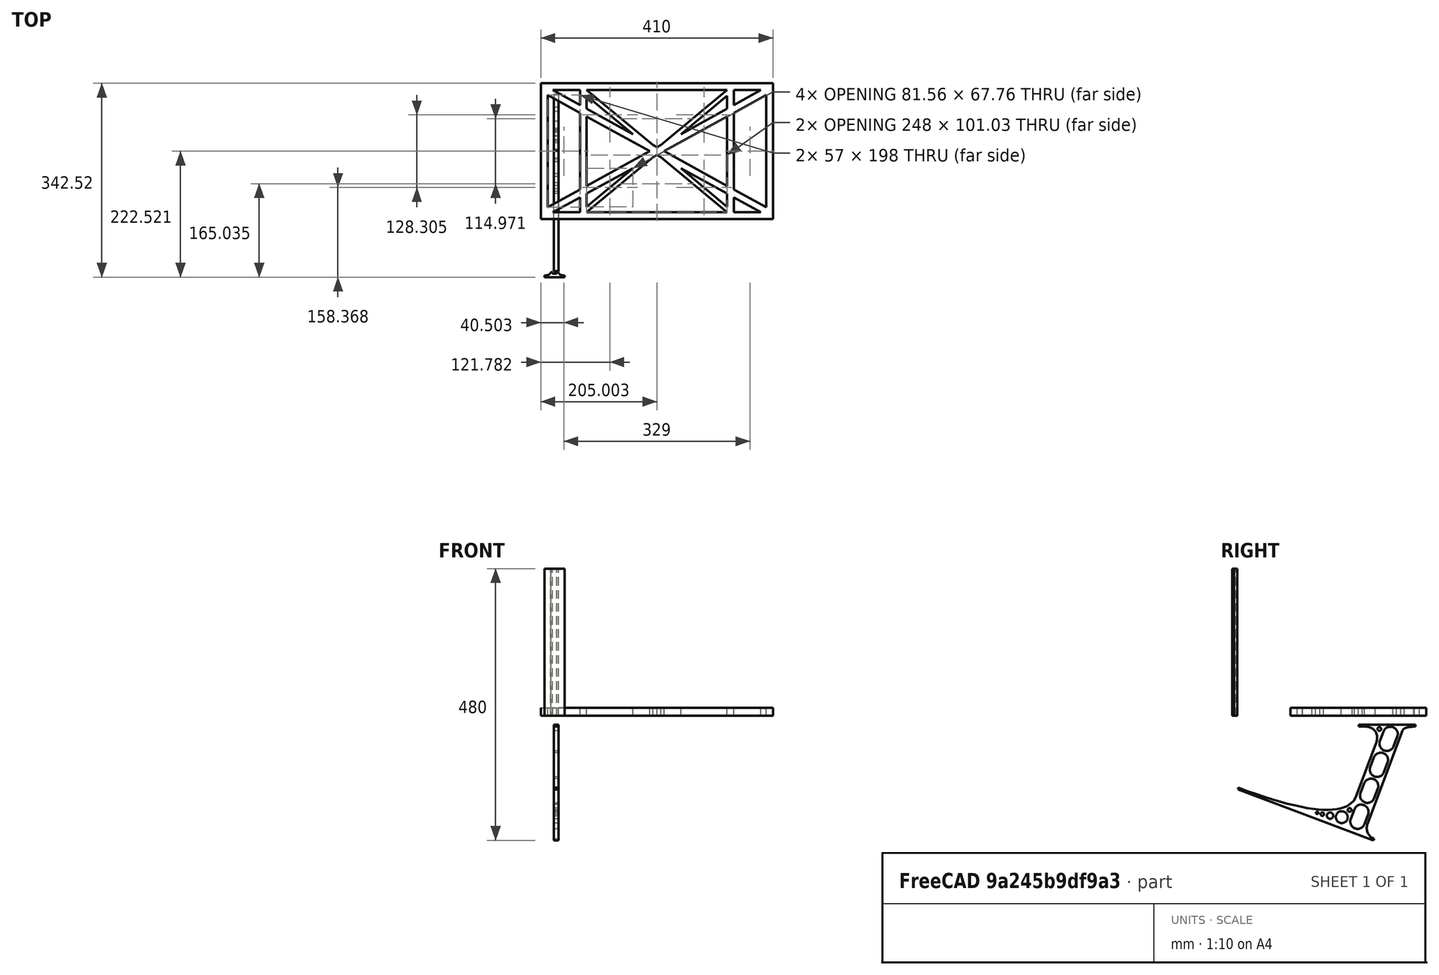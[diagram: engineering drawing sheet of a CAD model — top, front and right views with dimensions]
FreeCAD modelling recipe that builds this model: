
FCSTD DOCUMENT  (FreeCAD 0.19R0.19.2)
Label: laptopStand043
License: All rights reserved
LicenseURL: http://en.wikipedia.org/wiki/All_rights_reserved
objects: Sketcher::SketchObject×3, Part::Extrusion×3
note: 6 computed .brp shape members not serialized (recipe doc carries the construction recipe); baked Part::Feature solids carry a one-line shape summary decoded from their .brp

FEATURE [Sketcher::SketchObject] Sketch
  FullyConstrained = false
  sketch-geometry (62):
    g0: LineSegment StartX=-22.9272 StartY=136.221 StartZ=0 EndX=387.073 EndY=136.221 EndZ=0
    g1: LineSegment StartX=-22.9272 StartY=-103.779 StartZ=0 EndX=387.073 EndY=-103.779 EndZ=0
    g2: LineSegment StartX=375.073 StartY=115.221 StartZ=0 EndX=318.073 EndY=83.9235 EndZ=0
    g3: LineSegment StartX=-10.9272 StartY=-82.7794 StartZ=0 EndX=46.0728 EndY=-51.4823 EndZ=0
    g4: LineSegment StartX=-1.92719 StartY=124.221 StartZ=0 EndX=46.0728 EndY=97.8651 EndZ=0
    g5: LineSegment StartX=366.073 StartY=-91.7794 StartZ=0 EndX=318.073 EndY=-65.424 EndZ=0
    g6: LineSegment StartX=-10.9272 StartY=115.221 StartZ=0 EndX=-10.9272 EndY=-82.7794 EndZ=0
    g7: LineSegment StartX=375.073 StartY=-82.7794 StartZ=0 EndX=375.073 EndY=115.221 EndZ=0
    g8: LineSegment StartX=-1.92719 StartY=-91.7794 StartZ=0 EndX=46.0728 EndY=-91.7794 EndZ=0
    g9: LineSegment StartX=318.073 StartY=124.221 StartZ=0 EndX=366.073 EndY=124.221 EndZ=0
    g10: LineSegment StartX=306.073 StartY=-81.8102 StartZ=0 EndX=224.513 EndY=-14.0532 EndZ=0
    g11: LineSegment StartX=58.0728 StartY=114.251 StartZ=0 EndX=139.632 EndY=46.4944 EndZ=0
    g12: LineSegment StartX=306.073 StartY=124.221 StartZ=0 EndX=189.124 EndY=27.0628 EndZ=0
    g13: LineSegment StartX=58.0728 StartY=-91.7794 StartZ=0 EndX=175.022 EndY=5.37834 EndZ=0
    g14: LineSegment StartX=46.0728 StartY=124.221 StartZ=0 EndX=46.0728 EndY=97.8651 EndZ=0
    g15: LineSegment StartX=58.0728 StartY=-81.8102 StartZ=0 EndX=58.0728 EndY=-58.8351 EndZ=0
    g16: LineSegment StartX=318.073 StartY=124.221 StartZ=0 EndX=318.073 EndY=97.8651 EndZ=0
    g17: LineSegment StartX=306.073 StartY=114.251 StartZ=0 EndX=306.073 EndY=91.2763 EndZ=0
    g18: LineSegment StartX=182.073 StartY=23.1914 StartZ=0 EndX=189.124 EndY=27.0628 EndZ=0
    g19: LineSegment StartX=182.073 StartY=9.24976 StartZ=0 EndX=175.022 EndY=5.37834 EndZ=0
    g20: LineSegment StartX=224.513 StartY=46.4944 StartZ=0 EndX=306.073 EndY=114.251 EndZ=0
    g21: LineSegment StartX=175.022 StartY=27.0628 StartZ=0 EndX=58.0728 EndY=124.221 EndZ=0
    g22: LineSegment StartX=169.377 StartY=16.2206 StartZ=0 EndX=58.0728 EndY=77.3346 EndZ=0
    g23: LineSegment StartX=139.632 StartY=-14.0532 StartZ=0 EndX=58.0728 EndY=-81.8102 EndZ=0
    g24: LineSegment StartX=194.768 StartY=16.2206 StartZ=0 EndX=306.073 EndY=-44.8935 EndZ=0
    g25: LineSegment StartX=224.513 StartY=46.4944 StartZ=0 EndX=306.073 EndY=91.2763 EndZ=0
    g26: LineSegment StartX=175.022 StartY=27.0628 StartZ=0 EndX=182.073 EndY=23.1914 EndZ=0
    g27: LineSegment StartX=139.632 StartY=-14.0532 StartZ=0 EndX=58.0728 EndY=-58.8351 EndZ=0
    g28: LineSegment StartX=189.124 StartY=5.37834 StartZ=0 EndX=182.073 EndY=9.24976 EndZ=0
    g29: LineSegment StartX=189.124 StartY=5.37834 StartZ=0 EndX=306.073 EndY=-91.7794 EndZ=0
    g30: LineSegment StartX=306.073 StartY=77.3346 StartZ=0 EndX=306.073 EndY=-44.8935 EndZ=0
    g31: LineSegment StartX=318.073 StartY=83.9235 StartZ=0 EndX=318.073 EndY=-51.4823 EndZ=0
    g32: LineSegment StartX=318.073 StartY=97.8651 StartZ=0 EndX=366.073 EndY=124.221 EndZ=0
    g33: LineSegment StartX=306.073 StartY=77.3346 StartZ=0 EndX=194.768 EndY=16.2206 EndZ=0
    g34: LineSegment StartX=306.073 StartY=-58.8351 StartZ=0 EndX=224.513 EndY=-14.0532 EndZ=0
    g35: LineSegment StartX=306.073 StartY=-58.8351 StartZ=0 EndX=306.073 EndY=-81.8102 EndZ=0
    g36: LineSegment StartX=318.073 StartY=-51.4823 StartZ=0 EndX=375.073 EndY=-82.7794 EndZ=0
    g37: LineSegment StartX=318.073 StartY=-65.424 StartZ=0 EndX=318.073 EndY=-91.7794 EndZ=0
    g38: LineSegment StartX=306.073 StartY=124.221 StartZ=0 EndX=58.0728 EndY=124.221 EndZ=0
    g39: LineSegment StartX=318.073 StartY=-91.7794 StartZ=0 EndX=366.073 EndY=-91.7794 EndZ=0
    g40: LineSegment StartX=58.0728 StartY=-91.7794 StartZ=0 EndX=306.073 EndY=-91.7794 EndZ=0
    g41: LineSegment StartX=58.0728 StartY=-44.8935 StartZ=0 EndX=58.0728 EndY=77.3346 EndZ=0
    g42: LineSegment StartX=46.0728 StartY=-65.424 StartZ=0 EndX=-1.92719 EndY=-91.7794 EndZ=0
    g43: LineSegment StartX=46.0728 StartY=-65.424 StartZ=0 EndX=46.0728 EndY=-91.7794 EndZ=0
    g44: LineSegment StartX=58.0728 StartY=-44.8935 StartZ=0 EndX=169.377 EndY=16.2206 EndZ=0
    g45: LineSegment StartX=58.0728 StartY=91.2763 StartZ=0 EndX=58.0728 EndY=114.251 EndZ=0
    g46: LineSegment StartX=46.0728 StartY=83.9235 StartZ=0 EndX=46.0728 EndY=-51.4823 EndZ=0
    g47: LineSegment StartX=46.0728 StartY=124.221 StartZ=0 EndX=-1.92719 EndY=124.221 EndZ=0
    g48: LineSegment StartX=58.0728 StartY=91.2763 StartZ=0 EndX=139.632 EndY=46.4944 EndZ=0
    g49: LineSegment StartX=46.0728 StartY=83.9235 StartZ=0 EndX=-10.9272 EndY=115.221 EndZ=0
    g50: LineSegment StartX=-22.9272 StartY=136.221 StartZ=0 EndX=-42.9272 EndY=136.221 EndZ=0
    g51: LineSegment StartX=387.073 StartY=136.221 StartZ=0 EndX=407.073 EndY=136.221 EndZ=0
    g52: LineSegment StartX=-42.9272 StartY=136.221 StartZ=0 EndX=-42.9272 EndY=-103.779 EndZ=0
    g53: LineSegment StartX=-22.9272 StartY=-103.779 StartZ=0 EndX=-42.9272 EndY=-103.779 EndZ=0
    g54: LineSegment StartX=407.073 StartY=136.221 StartZ=0 EndX=407.073 EndY=-103.779 EndZ=0
    g55: LineSegment StartX=387.073 StartY=-103.779 StartZ=0 EndX=407.073 EndY=-103.779 EndZ=0
    g56: LineSegment StartX=175.022 StartY=27.0628 StartZ=0 EndX=179.022 EndY=27.0628 EndZ=0
    g57: LineSegment StartX=189.124 StartY=27.0628 StartZ=0 EndX=185.124 EndY=27.0628 EndZ=0
    g58: LineSegment StartX=179.022 StartY=27.0628 StartZ=0 EndX=179.022 EndY=127.888 EndZ=0
    g59: LineSegment StartX=185.124 StartY=27.0628 StartZ=0 EndX=185.124 EndY=128.758 EndZ=0
    g60: LineSegment StartX=179.022 StartY=27.0628 StartZ=0 EndX=179.022 EndY=-96.912 EndZ=0
    g61: LineSegment StartX=185.124 StartY=27.0628 StartZ=0 EndX=185.124 EndY=-96.1104 EndZ=0
  constraints (127):
    c: Horizontal(g0)
    c: Distance(g0) = 410
    c: Horizontal(g1)
    c: Block(g0)
    c: Horizontal(g8)
    c: Horizontal(g9)
    c: PointOnObject(g33,g4)
    c: Coincident(g26,g18)
    c: Coincident(g28,g19)
    c: Tangent(g5,g22)
    c: PointOnObject(g22,g3)
    c: PointOnObject(g24,g2)
    c: Coincident(g18,g12)
    c: Tangent(g18,g25)
    c: Coincident(g48,g11)
    c: Coincident(g26,g21)
    c: Coincident(g20,g25)
    c: Coincident(g19,g13)
    c: Coincident(g27,g23)
    c: Tangent(g19,g27)
    c: Coincident(g34,g10)
    c: Coincident(g29,g28)
    c: Coincident(g20,g17)
    c: Tangent(g17,g30)
    c: Tangent(g16,g31)
    c: Coincident(g25,g17)
    c: Tangent(g25,g32)
    c: Coincident(g2,g31)
    c: Coincident(g33,g30)
    c: Tangent(g2,g33)
    c: Coincident(g35,g10)
    c: Tangent(g5,g34)
    c: Tangent(g30,g35)
    c: Coincident(g24,g30)
    c: Tangent(g24,g36)
    c: Coincident(g31,g36)
    c: Coincident(g37,g5)
    c: Tangent(g31,g37)
    c: Coincident(g23,g15)
    c: Tangent(g15,g41)
    c: Coincident(g27,g15)
    c: Tangent(g27,g42)
    c: Coincident(g43,g42)
    c: Tangent(g14,g43)
    c: Coincident(g3,g46)
    c: Coincident(g44,g41)
    c: Tangent(g3,g44)
    c: Tangent(g41,g45)
    c: Tangent(g14,g46)
    c: Coincident(g11,g45)
    c: PointOnObject(g38,g21)
    c: Tangent(g38,g47)
    c: Coincident(g4,g14)
    c: Coincident(g48,g45)
    c: Tangent(g4,g48)
    c: Coincident(g22,g41)
    c: Coincident(g49,g46)
    c: Tangent(g22,g49)
    c: Block(g21)
    c: Block(g12)
    c: Block(g18)
    c: Block(g38)
    c: Block(g16)
    c: Block(g32)
    c: Block(g2)
    c: Block(g36)
    c: Block(g7)
    c: Block(g34)
    c: Block(g35)
    c: Block(g5)
    c: Block(g37)
    c: Block(g20)
    c: Block(g29)
    c: Block(g40)
    c: Block(g19)
    c: Block(g13)
    c: Block(g27)
    c: Block(g23)
    c: Block(g43)
    c: Block(g42)
    c: Block(g3)
    c: Block(g6)
    c: Block(g49)
    c: Block(g4)
    c: Block(g14)
    c: Block(g11)
    c: Block(g45)
    c: Block(g33)
    c: Block(g30)
    c: Block(g22)
    c: Block(g44)
    c: Block(g47)
    c: Block(g9)
    c: Block(g39)
    c: Block(g8)
    c: Horizontal(g50)
    c: Distance(g50) = 20
    c: Coincident(g51,g0)
    c: Horizontal(g51)
    c: Distance(g51) = 20
    c: Coincident(g52,g50)
    c: Vertical(g52)
    c: Horizontal(g53)
    c: Coincident(g53,g52)
    c: Coincident(g54,g51)
    c: Vertical(g54)
    c: Coincident(g55,g1)
    c: Horizontal(g55)
    c: Coincident(g55,g54)
    c: Block(g54)
    c: Block(g53)
    c: Block(g52)
    c: Block(g1)
    c: Coincident(g56,g21)
    c: Horizontal(g56)
    c: Distance(g56) = 4
    c: Coincident(g57,g12)
    c: Horizontal(g57)
    c: Distance(g57) = 4
    c: Coincident(g58,g56)
    c: Vertical(g58)
    c: Coincident(g59,g57)
    c: Vertical(g59)
    c: Coincident(g60,g56)
    c: Vertical(g60)
    c: Coincident(g61,g57)
    c: Vertical(g61)
FEATURE [Sketcher::SketchObject] Sketch001
  FullyConstrained = true
  MapMode = 4
  Placement = pos=(0,0,0) rot=(0.57735,0.57735,0.57735;2.0944rad)
  Support = -> [Sketch]
  sketch-geometry (46):
    g0: BSplineCurve PolesCount=3 KnotsCount=2 Degree=2 IsPeriodic=0
    g1: ArcOfCircle CenterX=73.122 CenterY=-32.2909 CenterZ=0 NormalX=0 NormalY=0 NormalZ=1 AngleXU=0 Radius=13 StartAngle=5.92268 EndAngle=9.06428
    g2: ArcOfCircle CenterX=66.7816 CenterY=-49.1439 CenterZ=0 NormalX=0 NormalY=0 NormalZ=1 AngleXU=0 Radius=13 StartAngle=2.78068 EndAngle=5.92131
    g3: ArcOfCircle CenterX=55.9263 CenterY=-78.1807 CenterZ=0 NormalX=0 NormalY=0 NormalZ=1 AngleXU=0 Radius=13 StartAngle=5.92268 EndAngle=9.06428
    g4: ArcOfCircle CenterX=49.5884 CenterY=-95.0342 CenterZ=0 NormalX=0 NormalY=0 NormalZ=1 AngleXU=0 Radius=13 StartAngle=2.78068 EndAngle=5.92131
    g5: ArcOfCircle CenterX=38.7206 CenterY=-124.067 CenterZ=0 NormalX=0 NormalY=0 NormalZ=1 AngleXU=0 Radius=13 StartAngle=5.92268 EndAngle=9.06428
    g6: ArcOfCircle CenterX=32.3875 CenterY=-140.92 CenterZ=0 NormalX=0 NormalY=0 NormalZ=1 AngleXU=0 Radius=13 StartAngle=2.78068 EndAngle=5.92131
    g7: ArcOfCircle CenterX=21.4715 CenterY=-169.934 CenterZ=0 NormalX=0 NormalY=0 NormalZ=1 AngleXU=0 Radius=13 StartAngle=5.92268 EndAngle=9.06428
    g8: ArcOfCircle CenterX=15.1336 CenterY=-186.787 CenterZ=0 NormalX=0 NormalY=0 NormalZ=1 AngleXU=0 Radius=13 StartAngle=2.78068 EndAngle=5.92131
    g9-g12: Circle x4 (B-spline internal-alignment scaffolding for g13; pole/knot coordinates omitted)
    g13: BSplineCurve PolesCount=4 KnotsCount=2 Degree=3 IsPeriodic=0
    g14: GeomPoint X=28.8094 Y=-19.0875 Z=0
    g15: GeomPoint X=47.0443 Y=-50.4712 Z=0
    g16: Circle CenterX=53.5586 CenterY=-23.2695 CenterZ=0 NormalX=0 NormalY=0 NormalZ=1 AngleXU=0 Radius=3.24518
    g17: Circle CenterX=-195.441 CenterY=-127.082 CenterZ=0 NormalX=0 NormalY=0 NormalZ=1 AngleXU=0 Radius=1
    g18: Circle CenterX=-8.24091 CenterY=-197.481 CenterZ=0 NormalX=0 NormalY=0 NormalZ=1 AngleXU=0 Radius=1
    g19: Circle CenterX=12.8789 CenterY=-141.321 CenterZ=0 NormalX=0 NormalY=0 NormalZ=1 AngleXU=0 Radius=1
    g20: BSplineCurve PolesCount=3 KnotsCount=2 Degree=2 IsPeriodic=0
    g21: GeomPoint X=-195.441 Y=-127.082 Z=0
    g22: GeomPoint X=12.8789 Y=-141.321 Z=0
    g23: Circle CenterX=-12.8016 CenterY=-179.036 CenterZ=0 NormalX=0 NormalY=0 NormalZ=1 AngleXU=0 Radius=10.5072
    g24: Circle CenterX=0.933922 CenterY=-166.43 CenterZ=0 NormalX=0 NormalY=0 NormalZ=1 AngleXU=0 Radius=3.26661
    g25: Circle CenterX=-33.5518 CenterY=-176.44 CenterZ=0 NormalX=0 NormalY=0 NormalZ=1 AngleXU=0 Radius=5.64388
    g26: Circle CenterX=-47.2366 CenterY=-173.859 CenterZ=0 NormalX=0 NormalY=0 NormalZ=1 AngleXU=0 Radius=3.01653
    g27: Circle CenterX=-56.2595 CenterY=-171.456 CenterZ=0 NormalX=0 NormalY=0 NormalZ=1 AngleXU=0 Radius=2.12826
    g28: ArcOfCircle CenterX=51.2151 CenterY=-198.473 CenterZ=0 NormalX=0 NormalY=0 NormalZ=1 AngleXU=0 Radius=20 StartAngle=2.78189 EndAngle=4.35269
    g29: LineSegment StartX=32.4951 StartY=-191.433 StartZ=0 EndX=94.6577 EndY=-26.1351 EndZ=0
    g30: LineSegment StartX=43.1192 StartY=-220.001 StartZ=0 EndX=-196.497 EndY=-129.89 EndZ=0
    g31: LineSegment StartX=43.1192 StartY=-220.001 StartZ=0 EndX=44.1752 EndY=-217.193 EndZ=0
    g32: LineSegment StartX=117.223 StartY=-19.0875 StartZ=0 EndX=117.223 EndY=-16.0875 EndZ=0
    g33: LineSegment StartX=117.223 StartY=-16.0875 StartZ=0 EndX=17.2232 EndY=-16.0875 EndZ=0
    g34: LineSegment StartX=17.2232 StartY=-16.0875 StartZ=0 EndX=17.2232 EndY=-19.0875 EndZ=0
    g35: LineSegment StartX=28.8094 StartY=-19.0875 StartZ=0 EndX=17.2232 EndY=-19.0875 EndZ=0
    g36: LineSegment StartX=47.0443 StartY=-50.4712 StartZ=0 EndX=12.8789 EndY=-141.321 EndZ=0
    g37: LineSegment StartX=-195.441 StartY=-127.082 StartZ=0 EndX=-196.497 EndY=-129.89 EndZ=0
    g38: LineSegment StartX=85.2864 StartY=-36.8765 StartZ=0 EndX=78.9396 EndY=-53.7463 EndZ=0
    g39: LineSegment StartX=60.9577 StartY=-27.7052 StartZ=0 EndX=54.6191 EndY=-44.5532 EndZ=0
    g40: LineSegment StartX=68.0907 StartY=-82.7664 StartZ=0 EndX=61.7465 EndY=-99.6365 EndZ=0
    g41: LineSegment StartX=43.7619 StartY=-73.595 StartZ=0 EndX=37.426 EndY=-90.4435 EndZ=0
    g42: LineSegment StartX=50.885 StartY=-128.652 StartZ=0 EndX=44.5456 EndY=-145.522 EndZ=0
    g43: LineSegment StartX=26.5562 StartY=-119.481 StartZ=0 EndX=20.2251 EndY=-136.329 EndZ=0
    g44: LineSegment StartX=9.3071 StartY=-165.349 StartZ=0 EndX=2.97115 EndY=-182.197 EndZ=0
    g45: LineSegment StartX=33.6358 StartY=-174.52 StartZ=0 EndX=27.2917 EndY=-191.39 EndZ=0
  constraints (70):
    c: Block(g0)
    c: Block(g1)
    c: Block(g2)
    c: Block(g4)
    c: Block(g3)
    c: Block(g6)
    c: Block(g5)
    c: Block(g8)
    c: Block(g7)
    c: Weight(g9) = 1
    c: Equal(g9,g10)
    c: Equal(g9,g11)
    c: Equal(g9,g12)
    c: InternalAlignment(g9-g12 -> g13) x4
    c: InternalAlignment(g14,g13)
    c: InternalAlignment(g15,g13)
    c: Block(g16)
    c: Weight(g17) = 1
    c: Equal(g17,g18)
    c: Equal(g17,g19)
    c: InternalAlignment(g17,g20)
    c: InternalAlignment(g18,g20)
    c: InternalAlignment(g19,g20)
    c: InternalAlignment(g21,g20)
    c: InternalAlignment(g22,g20)
    c: Block(g20)
    c: Block(g23)
    c: Block(g24)
    c: Block(g25)
    c: Block(g26)
    c: Block(g27)
    c: Block(g28)
    c: Coincident(g29,g28)
    c: Coincident(g29,g0)
    c: Block(g13)
    c: Coincident(g31,g30)
    c: Coincident(g31,g28)
    c: Block(g31)
    c: Coincident(g32,g0)
    c: Vertical(g32)
    c: Coincident(g33,g32)
    c: Horizontal(g33)
    c: Coincident(g34,g33)
    c: Vertical(g34)
    c: Block(g33)
    c: Coincident(g35,g13)
    c: Coincident(g35,g34)
    c: Horizontal(g35)
    c: Coincident(g36,g13)
    c: Coincident(g36,g20)
    c: Coincident(g37,g20)
    c: Coincident(g37,g30)
    c: Block(g30)
    c: Coincident(g38,g1)
    c: Coincident(g38,g2)
    c: Coincident(g39,g1)
    c: Coincident(g39,g2)
    c: Coincident(g40,g3)
    c: Coincident(g40,g4)
    c: Coincident(g41,g3)
    c: Coincident(g41,g4)
    c: Coincident(g42,g5)
    c: Coincident(g42,g6)
    c: Coincident(g43,g5)
    c: Coincident(g43,g6)
    c: Coincident(g44,g7)
    c: Coincident(g44,g8)
    c: Coincident(g45,g7)
    c: Coincident(g45,g8)
    c: Distance(g30) = 256
FEATURE [Part::Extrusion] Extrude002
  Base = -> Sketch001
  Dir = (1,0,0)
  DirMode = 2
  FaceMakerClass = Part::FaceMakerBullseye
  LengthFwd = 8
  LengthRev = 0
  Solid = true
  Symmetric = false
FEATURE [Sketcher::SketchObject] Sketch002
  FullyConstrained = true
  sketch-geometry (20):
    g0: LineSegment StartX=-2.77179 StartY=-200.304 StartZ=0 EndX=5.22821 EndY=-200.304 EndZ=0
    g1: LineSegment StartX=5.22821 StartY=-200.304 StartZ=0 EndX=5.22821 EndY=-197.304 EndZ=0
    g2: LineSegment StartX=-2.77179 StartY=-200.304 StartZ=0 EndX=-2.77179 EndY=-197.304 EndZ=0
    g3: LineSegment StartX=5.22821 StartY=-197.304 StartZ=0 EndX=8.22821 EndY=-197.304 EndZ=0
    g4: LineSegment StartX=-2.77179 StartY=-197.304 StartZ=0 EndX=-5.77179 EndY=-197.304 EndZ=0
    g5: LineSegment StartX=19.2282 StartY=-203.304 StartZ=0 EndX=19.2282 EndY=-206.304 EndZ=0
    g6: LineSegment StartX=-16.7718 StartY=-203.304 StartZ=0 EndX=-16.7718 EndY=-206.304 EndZ=0
    g7: LineSegment StartX=-16.7718 StartY=-206.304 StartZ=0 EndX=19.2282 EndY=-206.304 EndZ=0
    g8: Circle CenterX=-16.7718 CenterY=-203.304 CenterZ=0 NormalX=0 NormalY=0 NormalZ=1 AngleXU=0 Radius=1
    g9: Circle CenterX=-5.77179 CenterY=-203.304 CenterZ=0 NormalX=0 NormalY=0 NormalZ=1 AngleXU=0 Radius=1
    g10: Circle CenterX=-5.77179 CenterY=-197.304 CenterZ=0 NormalX=0 NormalY=0 NormalZ=1 AngleXU=0 Radius=1
    g11: BSplineCurve PolesCount=3 KnotsCount=2 Degree=2 IsPeriodic=0
    g12: GeomPoint X=-16.7718 Y=-203.304 Z=0
    g13: GeomPoint X=-5.77179 Y=-197.304 Z=0
    g14: Circle CenterX=19.2282 CenterY=-203.304 CenterZ=0 NormalX=0 NormalY=0 NormalZ=1 AngleXU=0 Radius=1
    g15: Circle CenterX=8.22821 CenterY=-203.304 CenterZ=0 NormalX=0 NormalY=0 NormalZ=1 AngleXU=0 Radius=1
    g16: Circle CenterX=8.22821 CenterY=-197.304 CenterZ=0 NormalX=0 NormalY=0 NormalZ=1 AngleXU=0 Radius=1
    g17: BSplineCurve PolesCount=3 KnotsCount=2 Degree=2 IsPeriodic=0
    g18: GeomPoint X=19.2282 Y=-203.304 Z=0
    g19: GeomPoint X=8.22821 Y=-197.304 Z=0
  constraints (41):
    c: Horizontal(g0)
    c: Distance(g0) = 8
    c: Coincident(g1,g0)
    c: Vertical(g1)
    c: Distance(g1) = 3
    c: Coincident(g2,g0)
    c: Vertical(g2)
    c: Distance(g2) = 3
    c: Coincident(g3,g1)
    c: Horizontal(g3)
    c: Distance(g3) = 3
    c: Coincident(g4,g2)
    c: Horizontal(g4)
    c: Distance(g4) = 3
    c: Vertical(g5)
    c: Vertical(g6)
    c: Coincident(g7,g6)
    c: Coincident(g7,g5)
    c: Weight(g8) = 1
    c: Equal(g8,g9)
    c: Equal(g8,g10)
    c: Coincident(g11,g4)
    c: InternalAlignment(g8,g11)
    c: InternalAlignment(g9,g11)
    c: InternalAlignment(g10,g11)
    c: InternalAlignment(g12,g11)
    c: InternalAlignment(g13,g11)
    c: Coincident(g17,g5)
    c: Weight(g14) = 1
    c: Equal(g14,g15)
    c: Equal(g14,g16)
    c: Coincident(g17,g3)
    c: InternalAlignment(g14,g17)
    c: InternalAlignment(g15,g17)
    c: InternalAlignment(g16,g17)
    c: InternalAlignment(g18,g17)
    c: InternalAlignment(g19,g17)
    c: Block(g7)
    c: Block(g17)
    c: Block(g11)
    c: Block(g6)
FEATURE [Part::Extrusion] Extrude003
  Base = -> Sketch002
  Dir = (0,0,1)
  DirMode = 2
  FaceMakerClass = Part::FaceMakerBullseye
  LengthFwd = 260
  LengthRev = 0
  Solid = true
  Symmetric = false
FEATURE [Part::Extrusion] Extrude
  Base = -> Sketch
  Dir = (0,0,1)
  DirMode = 2
  FaceMakerClass = Part::FaceMakerBullseye
  LengthFwd = 14
  LengthRev = 0
  Solid = true
  Symmetric = false
